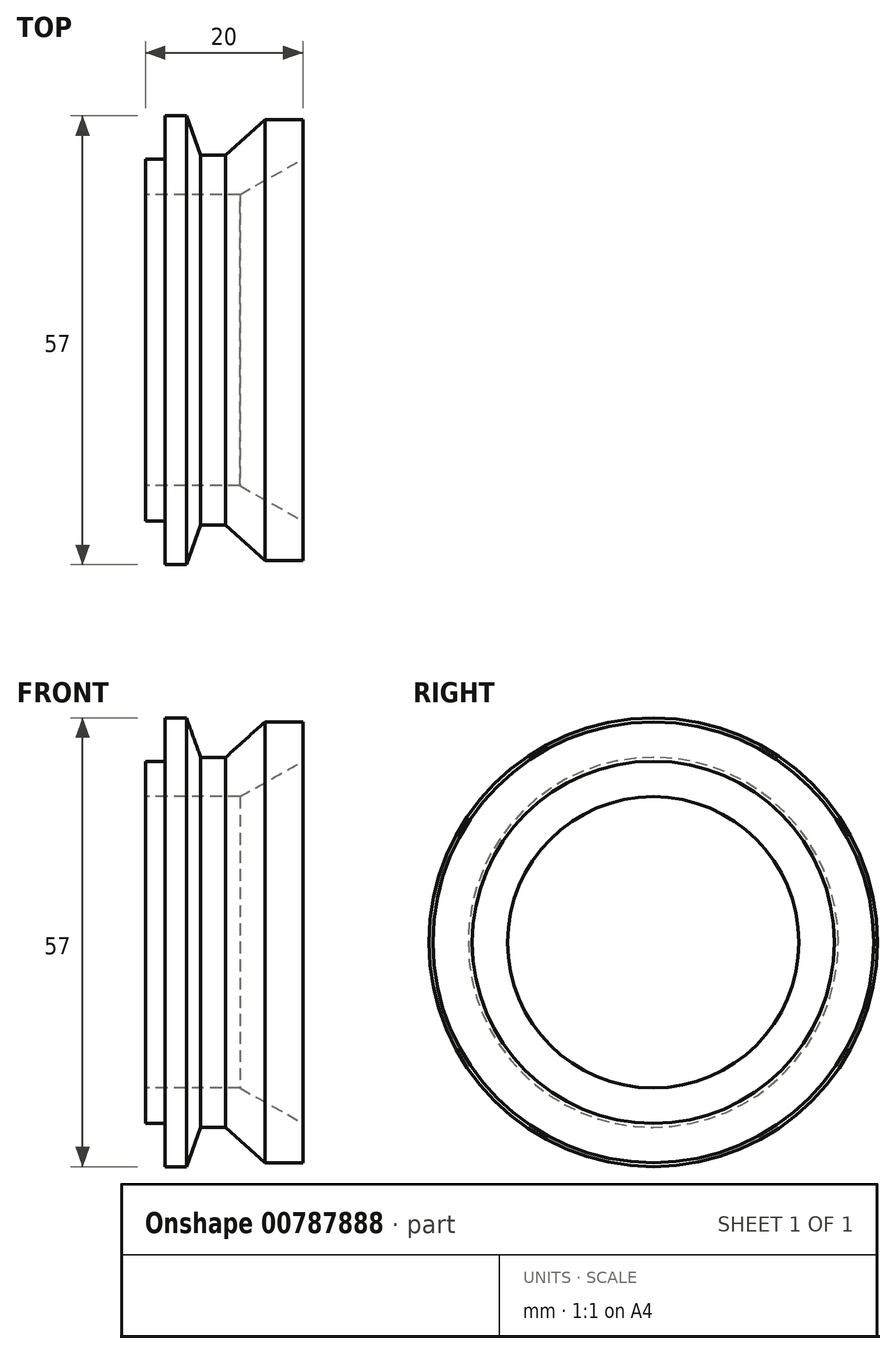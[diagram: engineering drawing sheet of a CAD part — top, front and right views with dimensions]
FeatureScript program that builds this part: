
annotation { "Feature Type Name" : "Feature", "Feature Type Description" : "" }
export const myFeature = defineFeature(function(context is Context, id is Id, definition is map)
    precondition{}
    {
        {
            var Q0;
            Q0=qCreatedBy(makeId("Front.planeOp"),FACE);
            var sketch = newSketch(context, id + "F0", { "sketchPlane" : qUnion([Q0])});
            skLineSegment(sketch, "E0", {"start": v(20, 23) * mm, "end": v(20, 28) * mm});
            skLineSegment(sketch, "E1", {"start": v(7.02, 23.5) * mm, "end": v(5.2, 28.5) * mm});
            skLineSegment(sketch, "E2", {"start": v(2.5, 23) * mm, "end": v(0, 23) * mm});
            skLineSegment(sketch, "E3", {"start": v(0, 23) * mm, "end": v(0, 18.5) * mm});
            skLineSegment(sketch, "E4", {"start": v(2.5, 23) * mm, "end": v(2.5, 28.5) * mm});
            skLineSegment(sketch, "E5", {"start": v(2.5, 28.5) * mm, "end": v(5.2, 28.5) * mm});
            skLineSegment(sketch, "E6", {"start": v(9.43, 29.85) * mm, "end": v(19.52, 29.85) * mm, "construction": true});
            skLineSegment(sketch, "E7", {"start": v(0, 0) * mm, "end": v(50.64, 0) * mm, "construction": true});
            skLineSegment(sketch, "E8", {"start": v(7.02, 23.5) * mm, "end": v(10.19, 23.5) * mm});
            skLineSegment(sketch, "E9", {"start": v(10.19, 23.5) * mm, "end": v(15.17, 28) * mm});
            skLineSegment(sketch, "E10", {"start": v(15.17, 28) * mm, "end": v(20, 28) * mm});
            skLineSegment(sketch, "E11", {"start": v(0, 18.5) * mm, "end": v(12, 18.5) * mm});
            skLineSegment(sketch, "E12", {"start": v(12, 18.5) * mm, "end": v(20, 23) * mm});
            skSolve(sketch);
        }
        {
            var Q0;
            Q0 = qSketchRegion(id + "F0", true);
            var Q1;
            Q1=sQuery(id+"F0.wireOp",EDGE,"E7");
            revolve(context, id + "F1", {"surfaceOperationType" : NewSurfaceOperationType.NEW, "entities" : qUnion([Q0]), "axis" : qUnion([Q1]), "revolveType" : RevolveType.FULL});
        }
    });
